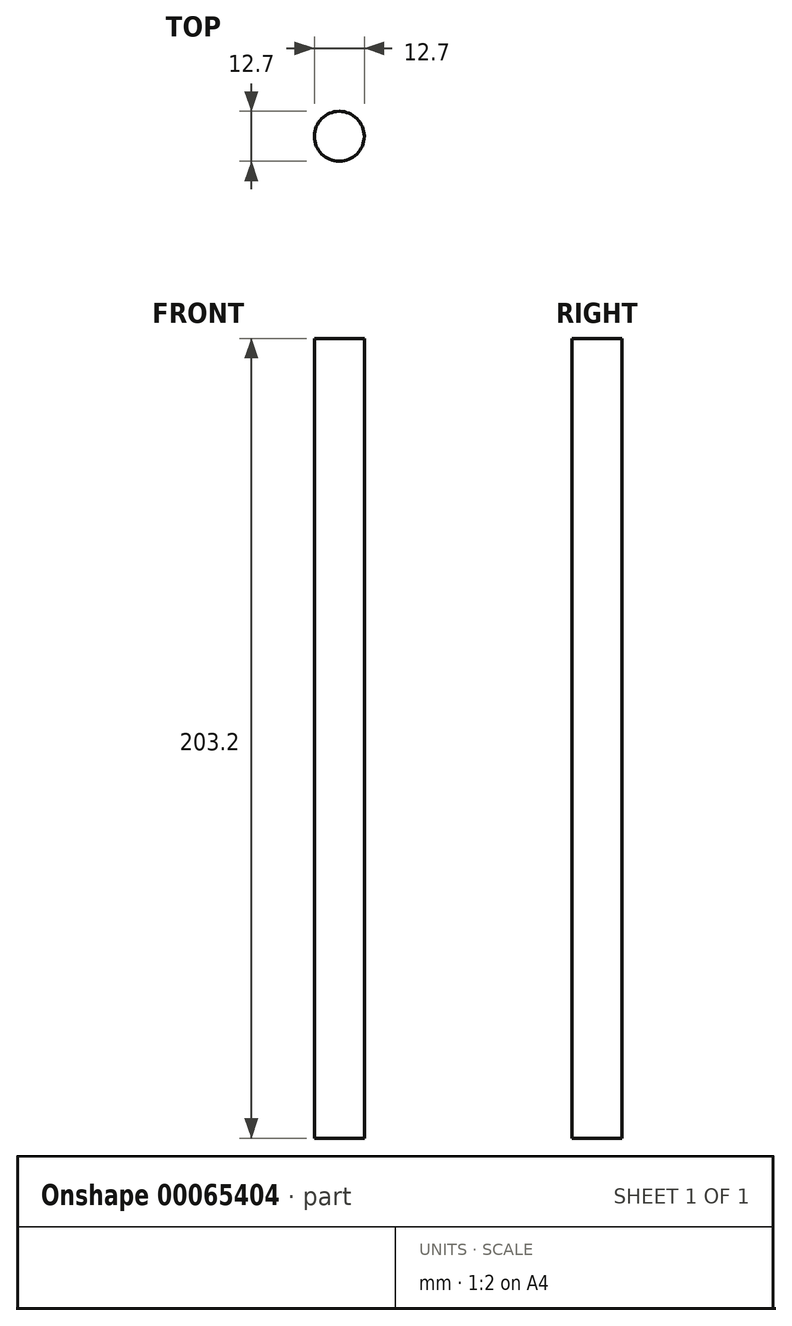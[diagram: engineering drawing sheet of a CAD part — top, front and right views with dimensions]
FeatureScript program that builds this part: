
annotation { "Feature Type Name" : "Feature", "Feature Type Description" : "" }
export const myFeature = defineFeature(function(context is Context, id is Id, definition is map)
    precondition{}
    {
        {
            var Q0;
            Q0=qCreatedBy(makeId("Top.planeOp"),FACE);
            var sketch = newSketch(context, id + "F0", { "sketchPlane" : qUnion([Q0])});
            skCircle(sketch, "E0", {"center": v(0, 0) * mm, "radius": 6.35 * mm});
            skSolve(sketch);
        }
        {
            var Q0;
            Q0=makeQuery(id+"F0.imprint","IMPRINT",FACE,{"disambiguationData":[TD([[makeQuery(id+"F0.imprint","IMPRINT",EDGE,{"derivedFrom":sQuery(id+"F0.wireOp",EDGE,"E0")}),1.0]])]});
            extrude(context, id + "F1", {"entities" : qUnion([Q0]), "depth" : 203.2 * mm});
        }
    });
